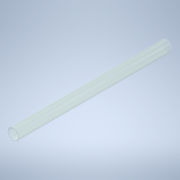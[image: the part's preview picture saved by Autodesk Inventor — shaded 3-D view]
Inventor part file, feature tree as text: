
AUTODESK INVENTOR PART (.ipt)
format: ipt  version: 2020 (Build 240168000, 168)  size: 97,280 bytes
history: native  units: mm
features: extrude x1, sketch x1
ambient origin geometry x8: Origin, YZ Plane, XZ Plane, XY Plane, X Axis, Y Axis, Z Axis, Center Point
bodies: Solid1 (feature_tree)
feature tree (2):
  extrude  "Extrusion1"  Depth=500.0mm
  sketch  "Sketch1"  dims[d0=32.0mm d1=2.0mm d2=500.0mm d3=0.0mm]
